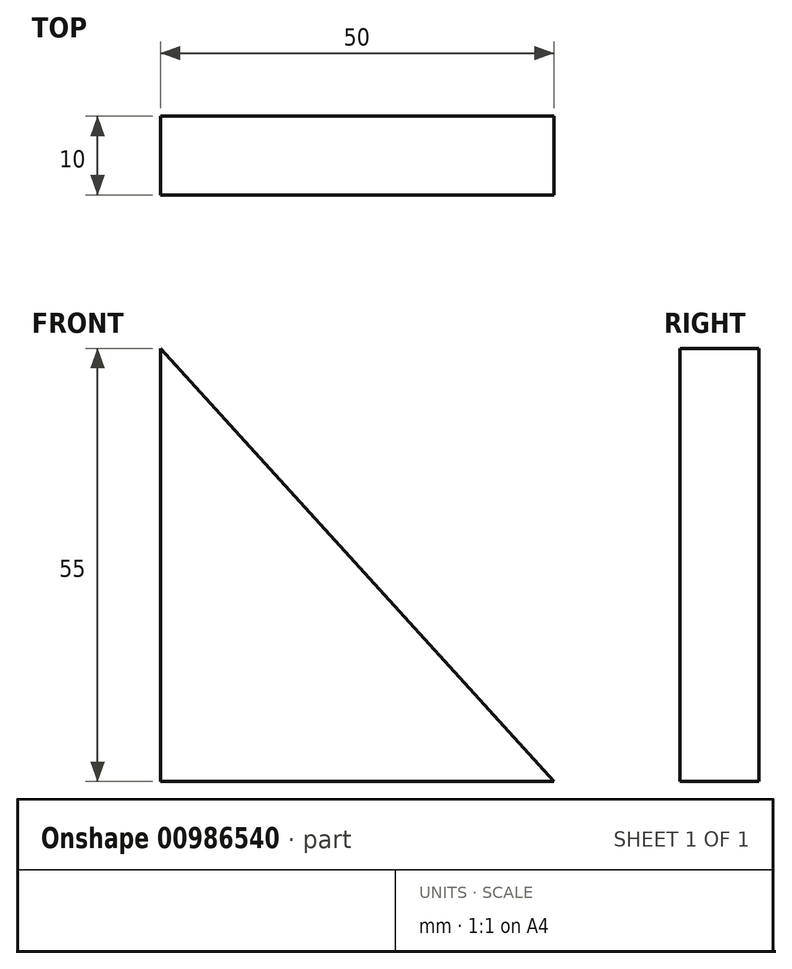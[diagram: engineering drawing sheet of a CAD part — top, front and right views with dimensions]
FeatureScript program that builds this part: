
annotation { "Feature Type Name" : "Feature", "Feature Type Description" : "" }
export const myFeature = defineFeature(function(context is Context, id is Id, definition is map)
    precondition{}
    {
        {
            var Q0;
            Q0=qCreatedBy(makeId("Front.planeOp"),FACE);
            var sketch = newSketch(context, id + "F0", { "sketchPlane" : qUnion([Q0])});
            skLineSegment(sketch, "E0", {"start": v(0, 0) * mm, "end": v(0, 55) * mm});
            skLineSegment(sketch, "E1", {"start": v(0, 55) * mm, "end": v(50, 0) * mm});
            skLineSegment(sketch, "E2", {"start": v(50, 0) * mm, "end": v(0, 0) * mm});
            skSolve(sketch);
        }
        {
            var Q0;
            Q0=makeQuery(id+"F0.imprint","IMPRINT",FACE,{"disambiguationData":[TD([[makeQuery(id+"F0.imprint","IMPRINT",EDGE,{"derivedFrom":sQuery(id+"F0.wireOp",EDGE,"E0")}),-1.0]])]});
            extrude(context, id + "F1", {"entities" : qUnion([Q0]), "depth" : 10 * mm, "offsetDistance" : 25 * mm});
        }
    });
